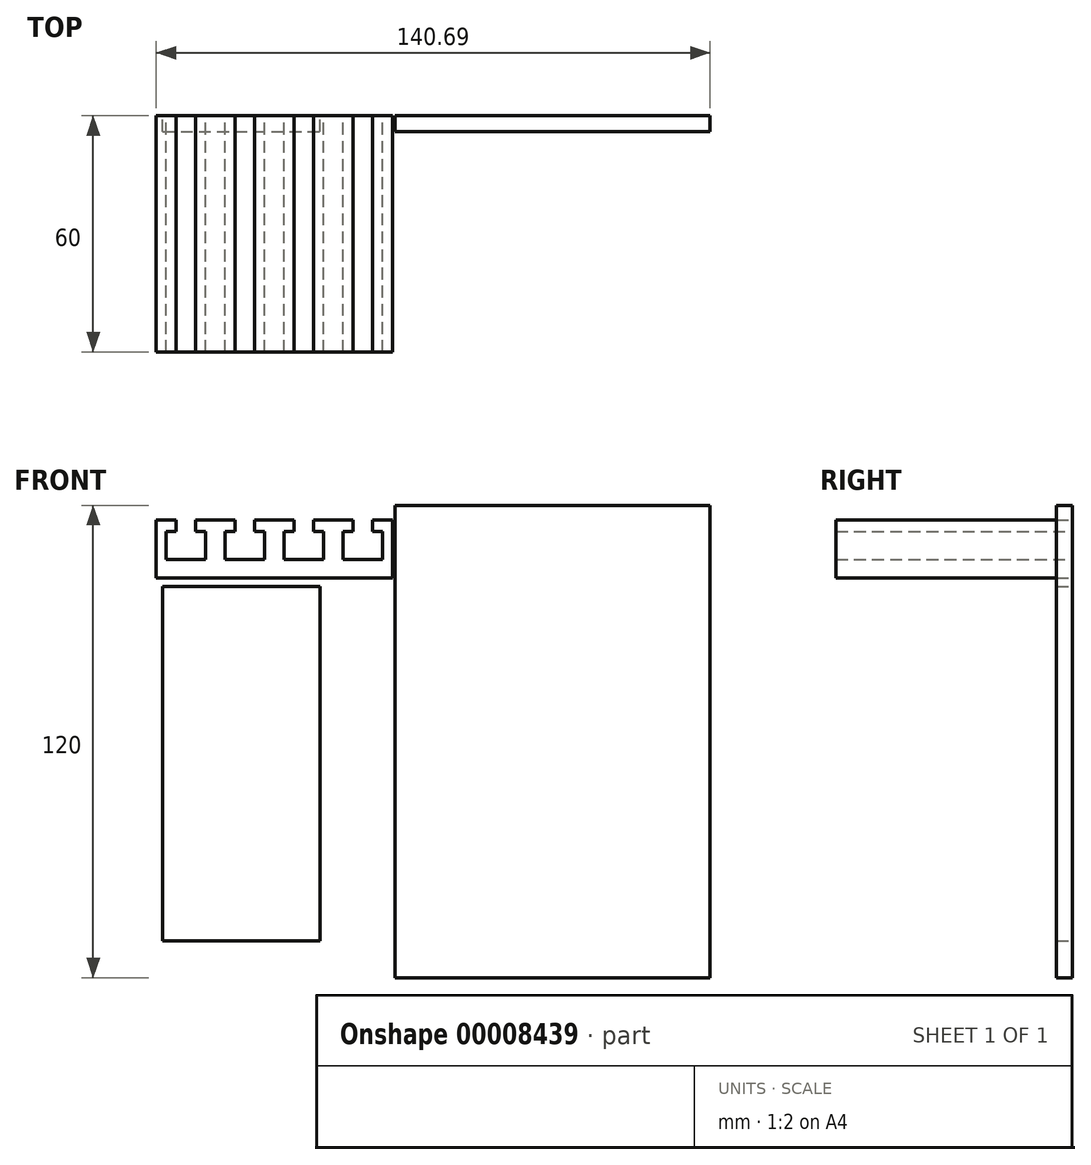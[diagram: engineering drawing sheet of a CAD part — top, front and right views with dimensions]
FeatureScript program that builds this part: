
annotation { "Feature Type Name" : "Feature", "Feature Type Description" : "" }
export const myFeature = defineFeature(function(context is Context, id is Id, definition is map)
    precondition{}
    {
        {
            var Q0;
            Q0=qCreatedBy(makeId("Front.planeOp"),FACE);
            var sketch = newSketch(context, id + "F0", { "sketchPlane" : qUnion([Q0])});
            skLineSegment(sketch, "E0", {"start": v(-55.6, 21.12) * mm, "end": v(-55.6, 35.8) * mm});
            skLineSegment(sketch, "E1", {"start": v(-55.6, 35.8) * mm, "end": v(-50.6, 35.8) * mm});
            skLineSegment(sketch, "E2", {"start": v(-50.6, 35.8) * mm, "end": v(-50.6, 32.9) * mm});
            skLineSegment(sketch, "E3", {"start": v(-50.6, 32.9) * mm, "end": v(-53.1, 32.9) * mm});
            skLineSegment(sketch, "E4", {"start": v(-53.1, 32.9) * mm, "end": v(-53.1, 25.77) * mm});
            skLineSegment(sketch, "E5", {"start": v(-53.1, 25.77) * mm, "end": v(-43.1, 25.77) * mm});
            skLineSegment(sketch, "E6", {"start": v(-43.1, 25.77) * mm, "end": v(-43.1, 32.9) * mm});
            skLineSegment(sketch, "E7", {"start": v(-43.1, 32.9) * mm, "end": v(-45.6, 32.9) * mm});
            skLineSegment(sketch, "E8", {"start": v(-45.6, 32.9) * mm, "end": v(-45.6, 35.8) * mm});
            skLineSegment(sketch, "E9", {"start": v(-45.6, 35.8) * mm, "end": v(-35.6, 35.8) * mm});
            skLineSegment(sketch, "E10", {"start": v(-35.6, 35.8) * mm, "end": v(-35.6, 32.9) * mm});
            skLineSegment(sketch, "E11", {"start": v(-35.6, 32.9) * mm, "end": v(-38.1, 32.9) * mm});
            skLineSegment(sketch, "E12", {"start": v(-38.1, 32.9) * mm, "end": v(-38.1, 25.77) * mm});
            skLineSegment(sketch, "E13", {"start": v(-38.1, 25.77) * mm, "end": v(-28.1, 25.77) * mm});
            skLineSegment(sketch, "E14", {"start": v(-28.1, 25.77) * mm, "end": v(-28.1, 32.9) * mm});
            skLineSegment(sketch, "E15", {"start": v(-28.1, 32.9) * mm, "end": v(-30.6, 32.9) * mm});
            skLineSegment(sketch, "E16", {"start": v(-30.6, 32.9) * mm, "end": v(-30.6, 35.8) * mm});
            skLineSegment(sketch, "E17", {"start": v(-30.6, 35.8) * mm, "end": v(-20.6, 35.8) * mm});
            skLineSegment(sketch, "E18", {"start": v(-20.6, 35.8) * mm, "end": v(-20.6, 32.9) * mm});
            skLineSegment(sketch, "E19", {"start": v(-20.6, 32.9) * mm, "end": v(-23.1, 32.9) * mm});
            skLineSegment(sketch, "E20", {"start": v(-23.1, 32.9) * mm, "end": v(-23.1, 25.77) * mm});
            skLineSegment(sketch, "E21", {"start": v(-23.1, 25.77) * mm, "end": v(-13.1, 25.77) * mm});
            skLineSegment(sketch, "E22", {"start": v(-13.1, 25.77) * mm, "end": v(-13.1, 32.9) * mm});
            skLineSegment(sketch, "E23", {"start": v(-13.1, 32.9) * mm, "end": v(-15.6, 32.9) * mm});
            skLineSegment(sketch, "E24", {"start": v(-15.6, 32.9) * mm, "end": v(-15.6, 35.8) * mm});
            skLineSegment(sketch, "E25", {"start": v(-15.6, 35.8) * mm, "end": v(-5.6, 35.8) * mm});
            skLineSegment(sketch, "E26", {"start": v(-5.6, 35.8) * mm, "end": v(-5.6, 32.9) * mm});
            skLineSegment(sketch, "E27", {"start": v(-5.6, 32.9) * mm, "end": v(-8.1, 32.9) * mm});
            skLineSegment(sketch, "E28", {"start": v(-8.1, 32.9) * mm, "end": v(-8.1, 25.77) * mm});
            skLineSegment(sketch, "E29", {"start": v(-8.1, 25.77) * mm, "end": v(1.9, 25.77) * mm});
            skLineSegment(sketch, "E30", {"start": v(1.9, 25.77) * mm, "end": v(1.9, 32.9) * mm});
            skLineSegment(sketch, "E31", {"start": v(1.9, 32.9) * mm, "end": v(-0.6, 32.9) * mm});
            skLineSegment(sketch, "E32", {"start": v(-0.6, 32.9) * mm, "end": v(-0.6, 35.8) * mm});
            skLineSegment(sketch, "E33", {"start": v(-0.6, 35.8) * mm, "end": v(4.4, 35.8) * mm});
            skLineSegment(sketch, "E34", {"start": v(4.4, 35.8) * mm, "end": v(4.4, 21.12) * mm});
            skLineSegment(sketch, "E35", {"start": v(-55.6, 21.12) * mm, "end": v(4.4, 21.12) * mm});
            skLineSegment(sketch, "E36", {"start": v(-53.1, 25.77) * mm, "end": v(-53.1, 21.12) * mm, "construction": true});
            skLineSegment(sketch, "E37", {"start": v(-38.1, 25.77) * mm, "end": v(-38.1, 21.12) * mm, "construction": true});
            skLineSegment(sketch, "E38", {"start": v(-23.1, 25.77) * mm, "end": v(-23.1, 21.12) * mm, "construction": true});
            skLineSegment(sketch, "E39", {"start": v(-8.1, 25.77) * mm, "end": v(-8.1, 21.12) * mm, "construction": true});
            skLineSegment(sketch, "E40", {"start": v(-50.6, 35.8) * mm, "end": v(-45.6, 35.8) * mm, "construction": true});
            skLineSegment(sketch, "E41", {"start": v(-35.6, 35.8) * mm, "end": v(-30.6, 35.8) * mm, "construction": true});
            skLineSegment(sketch, "E42", {"start": v(-20.6, 35.8) * mm, "end": v(-15.6, 35.8) * mm, "construction": true});
            skLineSegment(sketch, "E43", {"start": v(-5.6, 35.8) * mm, "end": v(-0.6, 35.8) * mm, "construction": true});
            skLineSegment(sketch, "E44", {"start": v(-43.1, 32.9) * mm, "end": v(-38.1, 32.9) * mm, "construction": true});
            skLineSegment(sketch, "E45", {"start": v(-28.1, 32.9) * mm, "end": v(-23.1, 32.9) * mm, "construction": true});
            skLineSegment(sketch, "E46", {"start": v(-13.1, 32.9) * mm, "end": v(-8.1, 32.9) * mm, "construction": true});
            skSolve(sketch);
        }
        {
            var Q0;
            Q0=makeQuery(id+"F0.imprint","IMPRINT",FACE,{"disambiguationData":[TD([[makeQuery(id+"F0.imprint","IMPRINT",EDGE,{"derivedFrom":sQuery(id+"F0.wireOp",EDGE,"E0")}),-1.0]])]});
            extrude(context, id + "F1", {"entities" : qUnion([Q0]), "depth" : 60 * mm});
        }
        {
            var Q0;
            Q0=qCreatedBy(makeId("Front.planeOp"),FACE);
            var sketch = newSketch(context, id + "F2", { "sketchPlane" : qUnion([Q0])});
            skLineSegment(sketch, "E47.bottom", {"start": v(-53.94, 18.93) * mm, "end": v(-13.94, 18.93) * mm});
            skLineSegment(sketch, "E47.top", {"start": v(-53.94, -71.07) * mm, "end": v(-13.94, -71.07) * mm});
            skLineSegment(sketch, "E47.left", {"start": v(-53.94, 18.93) * mm, "end": v(-53.94, -71.07) * mm});
            skLineSegment(sketch, "E47.right", {"start": v(-13.94, 18.93) * mm, "end": v(-13.94, -71.07) * mm});
            skSolve(sketch);
        }
        {
            var Q0;
            Q0=makeQuery(id+"F2.imprint","IMPRINT",FACE,{"disambiguationData":[TD([[makeQuery(id+"F2.imprint","IMPRINT",EDGE,{"derivedFrom":sQuery(id+"F2.wireOp",EDGE,"E47.bottom")}),-1.0]])]});
            extrude(context, id + "F3", {"entities" : qUnion([Q0]), "depth" : 4 * mm});
        }
        {
            var Q0;
            Q0=qCreatedBy(makeId("Front.planeOp"),FACE);
            var sketch = newSketch(context, id + "F4", { "sketchPlane" : qUnion([Q0])});
            skLineSegment(sketch, "E48.bottom", {"start": v(5.1, 39.54) * mm, "end": v(85.1, 39.54) * mm});
            skLineSegment(sketch, "E48.top", {"start": v(5.1, -80.46) * mm, "end": v(85.1, -80.46) * mm});
            skLineSegment(sketch, "E48.left", {"start": v(5.1, 39.54) * mm, "end": v(5.1, -80.46) * mm});
            skLineSegment(sketch, "E48.right", {"start": v(85.1, 39.54) * mm, "end": v(85.1, -80.46) * mm});
            skSolve(sketch);
        }
        {
            var Q0;
            Q0=makeQuery(id+"F4.imprint","IMPRINT",FACE,{"disambiguationData":[TD([[makeQuery(id+"F4.imprint","IMPRINT",EDGE,{"derivedFrom":sQuery(id+"F4.wireOp",EDGE,"E48.bottom")}),-1.0]])]});
            extrude(context, id + "F5", {"entities" : qUnion([Q0]), "depth" : 4 * mm});
        }
    });
